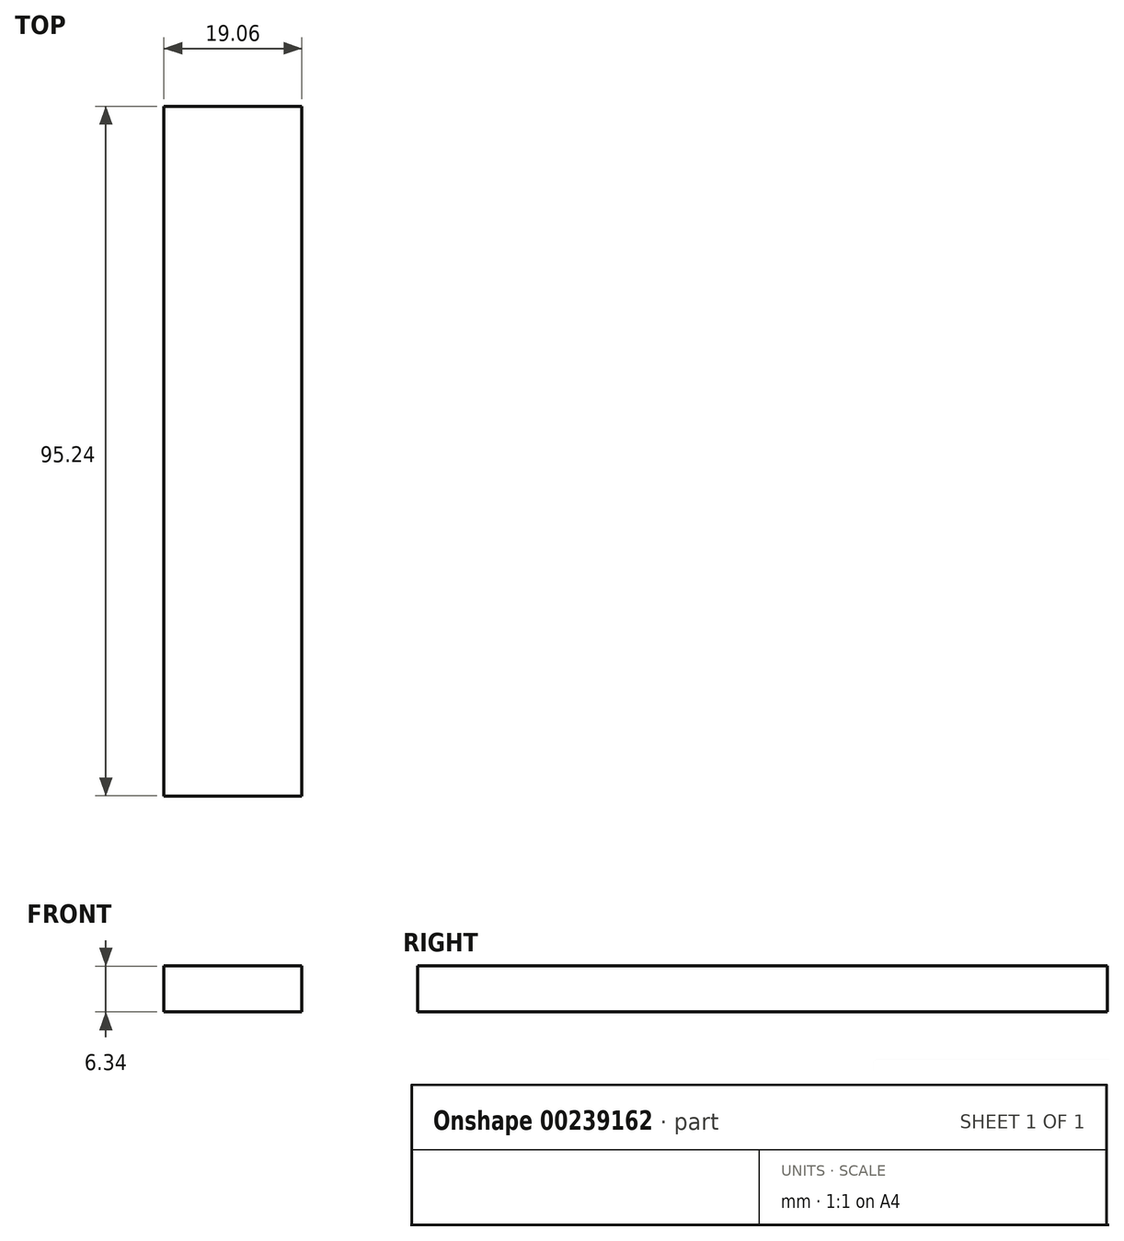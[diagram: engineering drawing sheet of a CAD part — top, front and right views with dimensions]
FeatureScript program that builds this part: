
annotation { "Feature Type Name" : "Feature", "Feature Type Description" : "" }
export const myFeature = defineFeature(function(context is Context, id is Id, definition is map)
    precondition{}
    {
        {
            var Q0;
            Q0=qCreatedBy(makeId("Front.planeOp"),FACE);
            var sketch = newSketch(context, id + "F0", { "sketchPlane" : qUnion([Q0])});
            skLineSegment(sketch, "E0.bottom", {"start": v(9.53, 3.18) * mm, "end": v(-9.53, 3.18) * mm});
            skLineSegment(sketch, "E0.top", {"start": v(9.53, -3.18) * mm, "end": v(-9.53, -3.18) * mm});
            skLineSegment(sketch, "E0.left", {"start": v(9.53, 3.18) * mm, "end": v(9.53, -3.18) * mm});
            skLineSegment(sketch, "E0.right", {"start": v(-9.53, 3.18) * mm, "end": v(-9.53, -3.18) * mm});
            skPoint(sketch, "E0.middle", {"position": v(0, 0) * mm});
            skSolve(sketch);
        }
        {
            var Q0;
            Q0 = qSketchRegion(id + "F0", true);
            extrude(context, id + "F1", {"entities" : qUnion([Q0]), "endBound" : BoundingType.SYMMETRIC, "depth" : 95.25 * mm});
        }
    });
